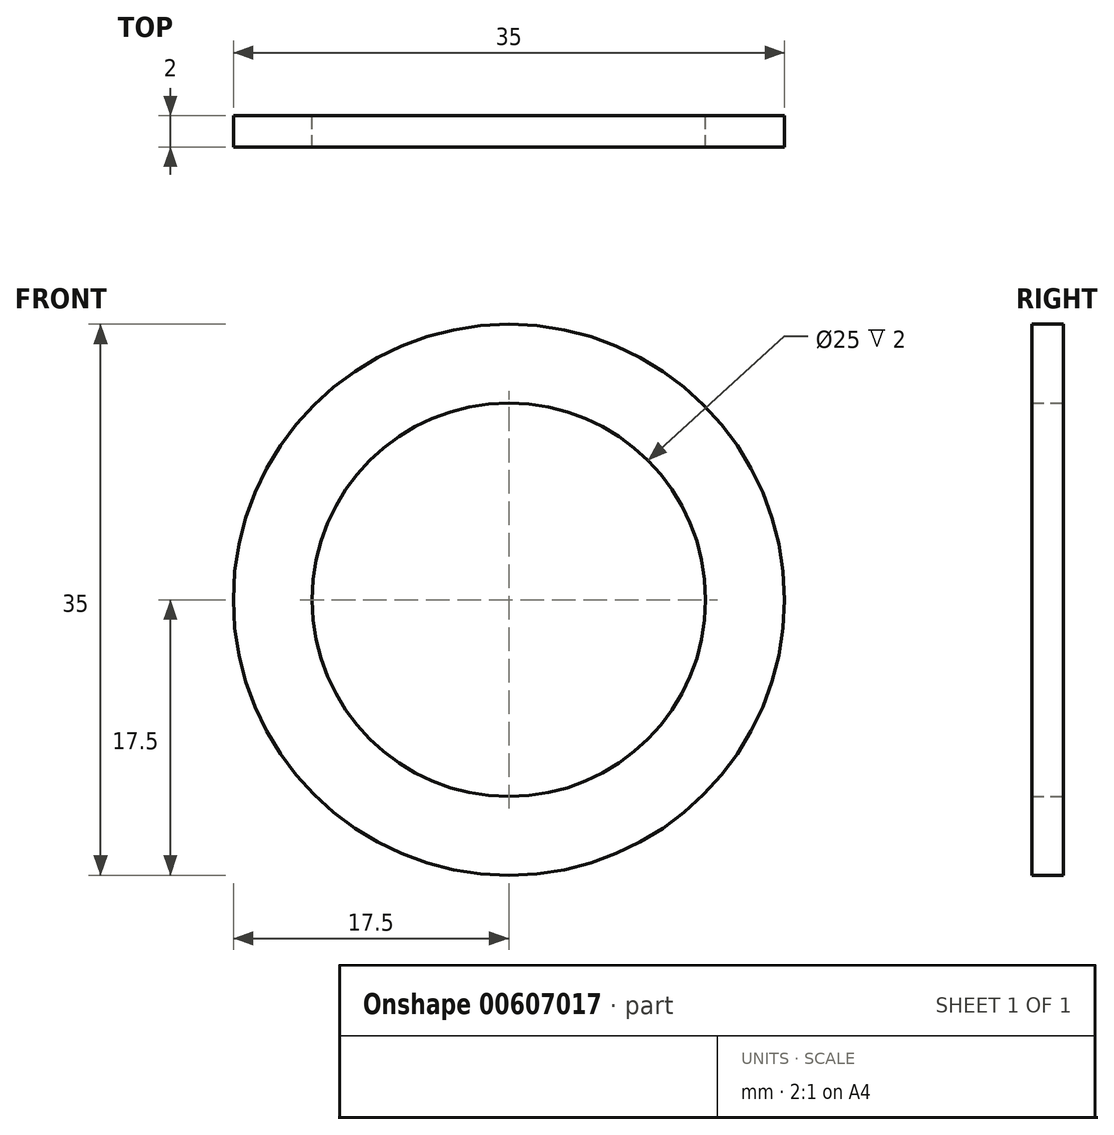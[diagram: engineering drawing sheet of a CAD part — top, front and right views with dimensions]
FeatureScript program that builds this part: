
annotation { "Feature Type Name" : "Feature", "Feature Type Description" : "" }
export const myFeature = defineFeature(function(context is Context, id is Id, definition is map)
    precondition{}
    {
        {
            var Q0;
            Q0=qCreatedBy(makeId("Front.planeOp"),FACE);
            var sketch = newSketch(context, id + "F0", { "sketchPlane" : qUnion([Q0]) });
            skCircle(sketch, "E0", {"center": v(0, 0) * mm, "radius": 17.5 * mm});
            skCircle(sketch, "E1", {"center": v(0, 0) * mm, "radius": 12.5 * mm});
            skSolve(sketch);
        }
        {
            var Q0;
            Q0=makeQuery(id+"F0.imprint","IMPRINT",FACE,{"disambiguationData":[TD([[makeQuery(id+"F0.imprint","IMPRINT",EDGE,{"derivedFrom":sQuery(id+"F0.wireOp",EDGE,"E0")}),1.0]])]});
            extrude(context, id + "F1", {"entities" : qUnion([Q0]), "depth" : 2 * mm, "offsetDistance" : 25 * mm});
        }
    });
